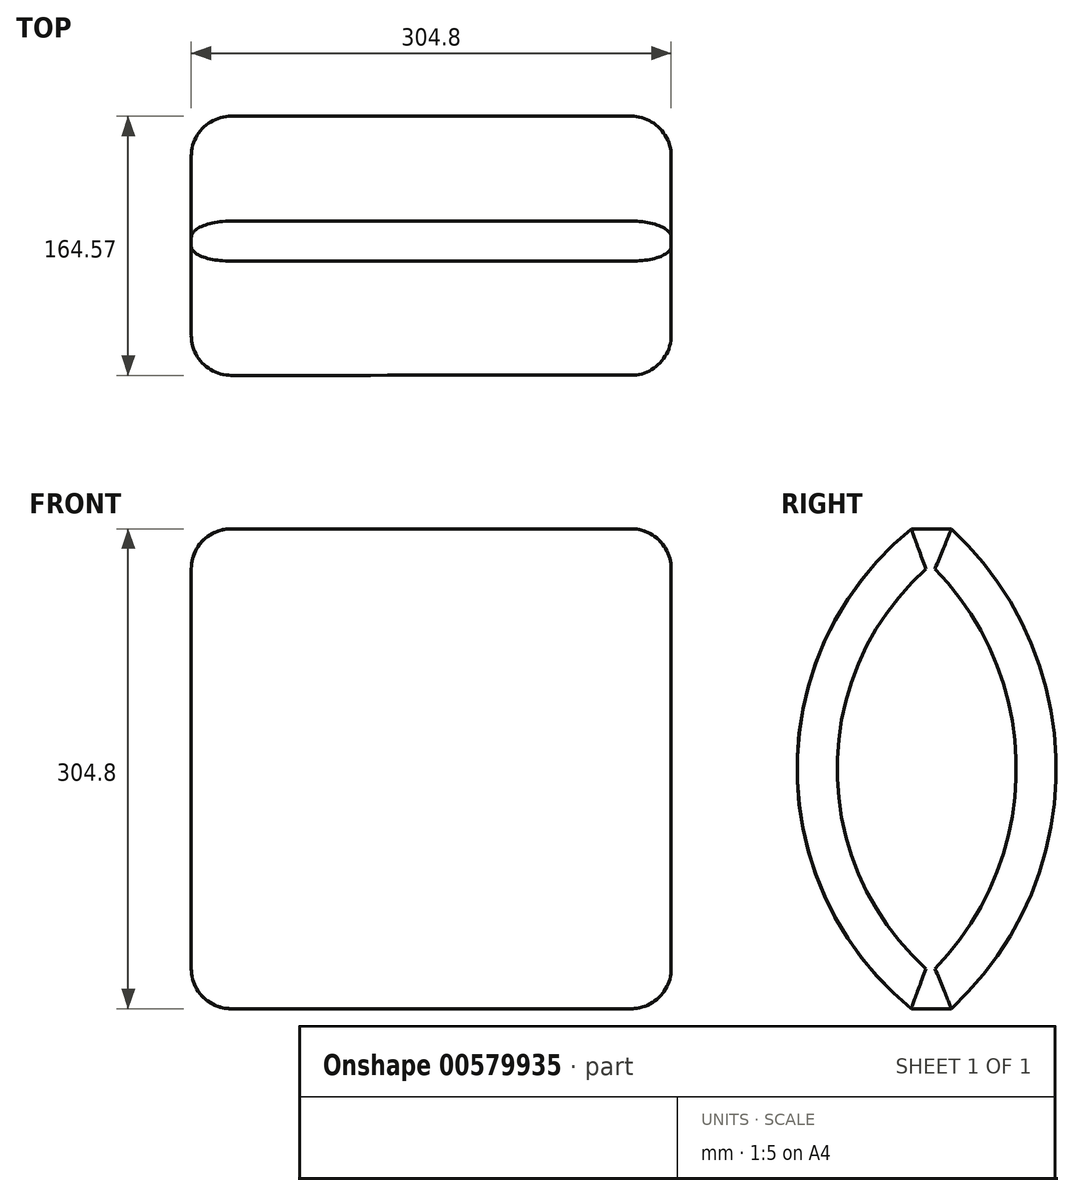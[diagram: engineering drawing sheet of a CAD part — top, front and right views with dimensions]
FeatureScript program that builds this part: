
annotation { "Feature Type Name" : "Feature", "Feature Type Description" : "" }
export const myFeature = defineFeature(function(context is Context, id is Id, definition is map)
    precondition{}
    {
        {
            var Q0;
            Q0=qCreatedBy(makeId("Front.planeOp"),FACE);
            var sketch = newSketch(context, id + "F0", { "sketchPlane" : qUnion([Q0])});
            skLineSegment(sketch, "E0.bottom", {"start": v(-177.45, 153.3) * mm, "end": v(127.35, 153.3) * mm});
            skLineSegment(sketch, "E0.top", {"start": v(-177.45, -151.5) * mm, "end": v(127.35, -151.5) * mm});
            skLineSegment(sketch, "E0.left", {"start": v(-177.45, 153.3) * mm, "end": v(-177.45, -151.5) * mm});
            skLineSegment(sketch, "E0.right", {"start": v(127.35, 153.3) * mm, "end": v(127.35, -151.5) * mm});
            skSolve(sketch);
        }
        {
            var Q0;
            Q0 = qSketchRegion(id + "F0", true);
            extrude(context, id + "F1", {"entities" : qUnion([Q0]), "depth" : 25.4 * mm, "offsetDistance" : 25.4 * mm});
        }
        {
            var Q0;
            Q0=makeQuery(id+"F1.opExtrude","SWEPT_FACE",FACE,{"disambiguationData":[OSD([sQuery(id+"F0.wireOp",EDGE,"E0.right")])]});
            var sketch = newSketch(context, id + "F2", { "sketchPlane" : qUnion([Q0])});
            skArc(sketch, "E1", {"start": v(0, -151.5) * mm, "mid": v(66.62, 0.9) * mm, "end": v(0, 153.3) * mm});
            skSolve(sketch);
        }
        {
            var Q0;
            Q0=makeQuery(id+"F1.opExtrude","SWEPT_FACE",FACE,{"disambiguationData":[OSD([sQuery(id+"F0.wireOp",EDGE,"E0.left")])]});
            var sketch = newSketch(context, id + "F3", { "sketchPlane" : qUnion([Q0])});
            skArc(sketch, "E2", {"start": v(0, 153.3) * mm, "mid": v(-66.6, 0.9) * mm, "end": v(0, -151.5) * mm});
            skSolve(sketch);
        }
        {
            var Q1;
            Q1=makeQuery(id+"F3.imprint","IMPRINT",FACE,{"disambiguationData":[TD([[makeQuery(id+"F3.imprint","IMPRINT",EDGE,{"derivedFrom":sQuery(id+"F3.wireOp",EDGE,"E2")}),1.0]])]});
            var Q2;
            Q2=makeQuery(id+"F2.imprint","IMPRINT",FACE,{"disambiguationData":[TD([[makeQuery(id+"F2.imprint","IMPRINT",EDGE,{"derivedFrom":sQuery(id+"F2.wireOp",EDGE,"E1")}),1.0]])]});
            loft(context, id + "F4", {"operationType" : NewBodyOperationType.ADD, "sheetProfilesArray" : [{ "sheetProfileEntities" : qUnion([Q1]) }, { "sheetProfileEntities" : qUnion([Q2]) }]});
        }
        {
            var Q0;
            {var subQ0=sQuery(id+"F0.wireOp",EDGE,"E0.right");Q0=makeQuery(id+"F4.boolean.opBoolean","MERGE",FACE,{"derivedFrom":[makeQuery(id+"F1.opExtrude","SWEPT_FACE",FACE,{"disambiguationData":[OSD([subQ0])]}),makeQuery(id+"F4.opLoft","CAP_FACE",FACE,{"disambiguationData":[OSD([makeQuery(id+"F2.imprint","IMPRINT",FACE,{"disambiguationData":[TD([[makeQuery(id+"F2.imprint","IMPRINT",EDGE,{"derivedFrom":sQuery(id+"F2.wireOp",EDGE,"E1")}),1.0]])]})])],"isStart":true})]});}
            var sketch = newSketch(context, id + "F5", { "sketchPlane" : qUnion([Q0])});
            skArc(sketch, "E3", {"start": v(-25.4, 153.3) * mm, "mid": v(-97.92, 0.9) * mm, "end": v(-25.4, -151.5) * mm});
            skSolve(sketch);
        }
        {
            var Q0;
            {var subQ0=sQuery(id+"F0.wireOp",EDGE,"E0.left");Q0=makeQuery(id+"F4.boolean.opBoolean","MERGE",FACE,{"derivedFrom":[makeQuery(id+"F1.opExtrude","SWEPT_FACE",FACE,{"disambiguationData":[OSD([subQ0])]}),makeQuery(id+"F4.opLoft","CAP_FACE",FACE,{"disambiguationData":[OSD([makeQuery(id+"F3.imprint","IMPRINT",FACE,{"disambiguationData":[TD([[makeQuery(id+"F3.imprint","IMPRINT",EDGE,{"derivedFrom":sQuery(id+"F3.wireOp",EDGE,"E2")}),1.0]])]})])],"isStart":true})]});}
            var sketch = newSketch(context, id + "F6", { "sketchPlane" : qUnion([Q0])});
            skArc(sketch, "E4", {"start": v(25.4, -151.5) * mm, "mid": v(97.96, 0.9) * mm, "end": v(25.4, 153.3) * mm});
            skSolve(sketch);
        }
        {
            var Q1;
            Q1=makeQuery(id+"F5.imprint","IMPRINT",FACE,{"disambiguationData":[TD([[makeQuery(id+"F5.imprint","IMPRINT",EDGE,{"derivedFrom":sQuery(id+"F5.wireOp",EDGE,"E3")}),1.0]])]});
            var Q2;
            Q2=makeQuery(id+"F6.imprint","IMPRINT",FACE,{"disambiguationData":[TD([[makeQuery(id+"F6.imprint","IMPRINT",EDGE,{"derivedFrom":sQuery(id+"F6.wireOp",EDGE,"E4")}),1.0]])]});
            loft(context, id + "F7", {"operationType" : NewBodyOperationType.ADD, "sheetProfilesArray" : [{ "sheetProfileEntities" : qUnion([Q1]) }, { "sheetProfileEntities" : qUnion([Q2]) }]});
        }
        {
            var Q0;
            Q0=makeQuery(id+"F1.opExtrude","SWEPT_EDGE",EDGE,{"disambiguationData":[OSD([sQuery(id+"F0.wireOp",EDGE,"E0.bottom"),sQuery(id+"F0.wireOp",EDGE,"E0.left")])]});
            var Q1;
            Q1=makeQuery(id+"F1.opExtrude","SWEPT_EDGE",EDGE,{"disambiguationData":[OSD([sQuery(id+"F0.wireOp",EDGE,"E0.top"),sQuery(id+"F0.wireOp",EDGE,"E0.left")])]});
            var Q2;
            {var subQ0=sQuery(id+"F6.wireOp",EDGE,"E4");var subQ1=sQuery(id+"F0.wireOp",EDGE,"E0.left");var subQ2=makeQuery(id+"F1.opExtrude","CAP_EDGE",EDGE,{"disambiguationData":[OSD([subQ1])],"isStart":false});var subQ3=sQuery(id+"F0.wireOp",EDGE,"E0.top");var subQ4=sQuery(id+"F0.wireOp",EDGE,"E0.bottom");Q2=makeQuery(id+"F7.opLoft","MID_CAP_EDGE",EDGE,{"disambiguationData":[OSD([subQ4,subQ3,subQ1,subQ0]),TDD([makeQuery(id+"F6.imprint","INTERSECT",VERTEX,{"derivedFrom":[makeQuery(id+"F1.opExtrude","SWEPT_EDGE",EDGE,{"disambiguationData":[OSD([subQ4,subQ1])]}),subQ2,subQ0]}),makeQuery(id+"F6.imprint","INTERSECT",VERTEX,{"derivedFrom":[makeQuery(id+"F1.opExtrude","SWEPT_EDGE",EDGE,{"disambiguationData":[OSD([subQ3,subQ1])]}),subQ2,subQ0]}),makeQuery(id+"F6.imprint","IMPRINT",EDGE,{"derivedFrom":subQ0})])],"capPos":1.0});}
            var Q3;
            {var subQ0=sQuery(id+"F3.wireOp",EDGE,"E2");var subQ1=sQuery(id+"F0.wireOp",EDGE,"E0.left");var subQ2=makeQuery(id+"F1.opExtrude","CAP_EDGE",EDGE,{"disambiguationData":[OSD([subQ1])],"isStart":true});var subQ3=sQuery(id+"F0.wireOp",EDGE,"E0.top");var subQ4=sQuery(id+"F0.wireOp",EDGE,"E0.bottom");Q3=makeQuery(id+"F4.opLoft","MID_CAP_EDGE",EDGE,{"disambiguationData":[OSD([subQ4,subQ3,subQ1,subQ0]),TDD([makeQuery(id+"F3.imprint","INTERSECT",VERTEX,{"derivedFrom":[makeQuery(id+"F1.opExtrude","SWEPT_EDGE",EDGE,{"disambiguationData":[OSD([subQ4,subQ1])]}),subQ2,subQ0]}),makeQuery(id+"F3.imprint","INTERSECT",VERTEX,{"derivedFrom":[makeQuery(id+"F1.opExtrude","SWEPT_EDGE",EDGE,{"disambiguationData":[OSD([subQ3,subQ1])]}),subQ2,subQ0]}),makeQuery(id+"F3.imprint","IMPRINT",EDGE,{"derivedFrom":subQ0})])],"capPos":0.0});}
            var Q4;
            {var subQ0=sQuery(id+"F5.wireOp",EDGE,"E3");var subQ1=sQuery(id+"F0.wireOp",EDGE,"E0.right");var subQ2=makeQuery(id+"F1.opExtrude","CAP_EDGE",EDGE,{"disambiguationData":[OSD([subQ1])],"isStart":false});var subQ3=sQuery(id+"F0.wireOp",EDGE,"E0.top");var subQ4=sQuery(id+"F0.wireOp",EDGE,"E0.bottom");Q4=makeQuery(id+"F7.opLoft","MID_CAP_EDGE",EDGE,{"disambiguationData":[OSD([subQ4,subQ3,subQ1,subQ0]),TDD([makeQuery(id+"F5.imprint","INTERSECT",VERTEX,{"derivedFrom":[makeQuery(id+"F1.opExtrude","SWEPT_EDGE",EDGE,{"disambiguationData":[OSD([subQ4,subQ1])]}),subQ2,subQ0]}),makeQuery(id+"F5.imprint","INTERSECT",VERTEX,{"derivedFrom":[makeQuery(id+"F1.opExtrude","SWEPT_EDGE",EDGE,{"disambiguationData":[OSD([subQ3,subQ1])]}),subQ2,subQ0]}),makeQuery(id+"F5.imprint","IMPRINT",EDGE,{"derivedFrom":subQ0})])],"capPos":0.0});}
            var Q5;
            Q5=makeQuery(id+"F1.opExtrude","SWEPT_EDGE",EDGE,{"disambiguationData":[OSD([sQuery(id+"F0.wireOp",EDGE,"E0.bottom"),sQuery(id+"F0.wireOp",EDGE,"E0.right")])]});
            var Q6;
            {var subQ0=sQuery(id+"F2.wireOp",EDGE,"E1");var subQ1=sQuery(id+"F0.wireOp",EDGE,"E0.right");var subQ2=makeQuery(id+"F1.opExtrude","CAP_EDGE",EDGE,{"disambiguationData":[OSD([subQ1])],"isStart":true});var subQ3=sQuery(id+"F0.wireOp",EDGE,"E0.top");var subQ4=sQuery(id+"F0.wireOp",EDGE,"E0.bottom");Q6=makeQuery(id+"F4.opLoft","MID_CAP_EDGE",EDGE,{"disambiguationData":[OSD([subQ4,subQ3,subQ1,subQ0]),TDD([makeQuery(id+"F2.imprint","INTERSECT",VERTEX,{"derivedFrom":[makeQuery(id+"F1.opExtrude","SWEPT_EDGE",EDGE,{"disambiguationData":[OSD([subQ4,subQ1])]}),subQ2,subQ0]}),makeQuery(id+"F2.imprint","INTERSECT",VERTEX,{"derivedFrom":[makeQuery(id+"F1.opExtrude","SWEPT_EDGE",EDGE,{"disambiguationData":[OSD([subQ3,subQ1])]}),subQ2,subQ0]}),makeQuery(id+"F2.imprint","IMPRINT",EDGE,{"derivedFrom":subQ0})])],"capPos":1.0});}
            var Q7;
            Q7=makeQuery(id+"F1.opExtrude","SWEPT_EDGE",EDGE,{"disambiguationData":[OSD([sQuery(id+"F0.wireOp",EDGE,"E0.top"),sQuery(id+"F0.wireOp",EDGE,"E0.right")])]});
            fillet(context, id + "F8", {"entities" : qUnion([Q0, Q1, Q2, Q3, Q4, Q5, Q6, Q7]), "radius" : 25.4 * mm, "tangentPropagation" : true, "allowEdgeOverflow" : false});
        }
    });
